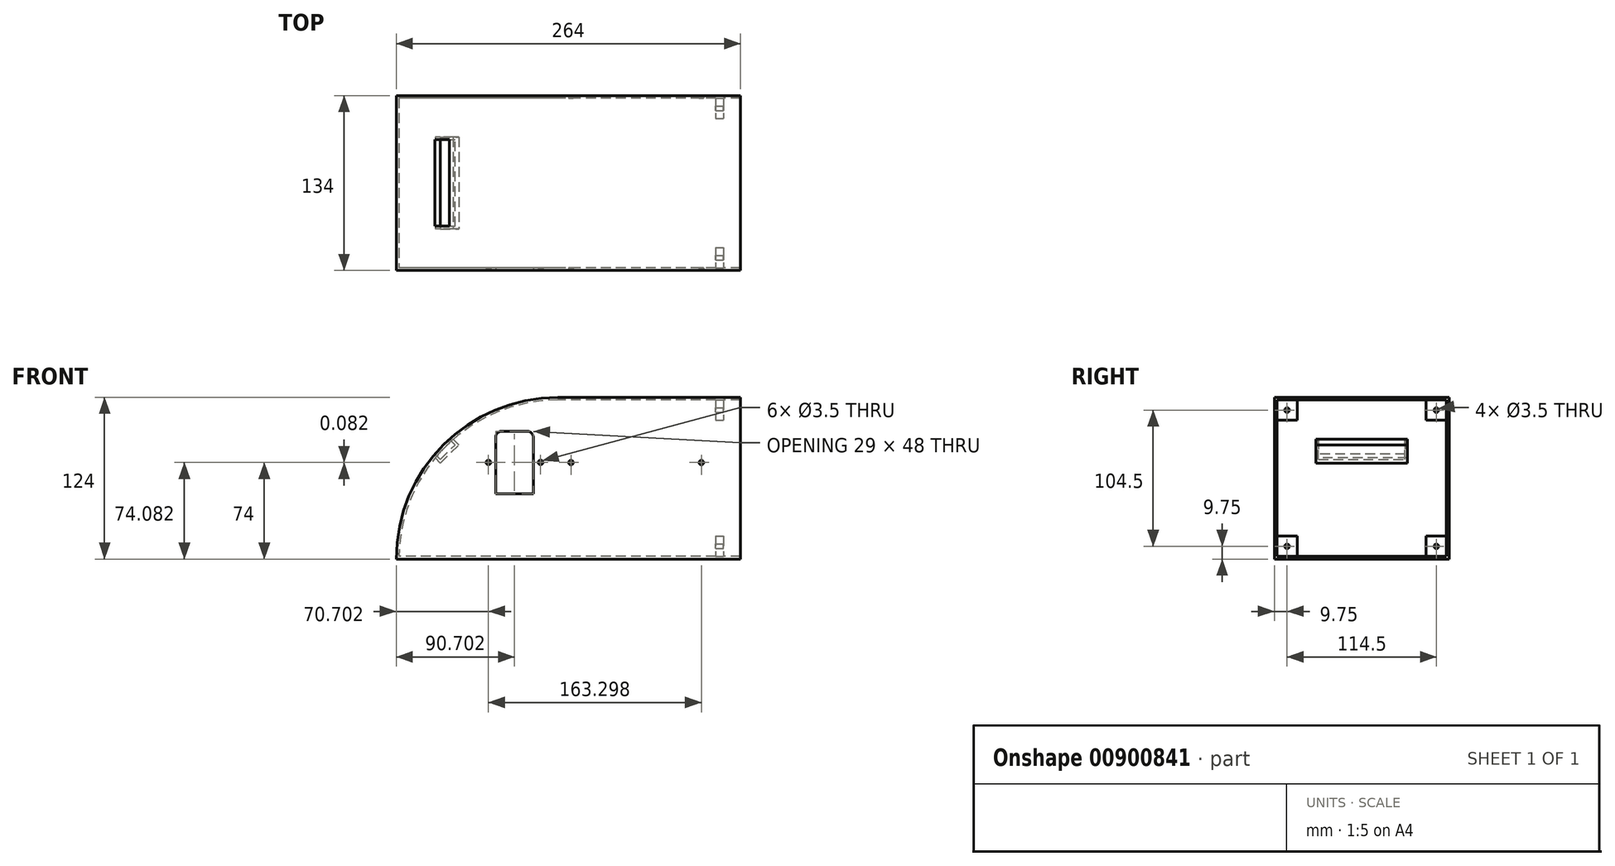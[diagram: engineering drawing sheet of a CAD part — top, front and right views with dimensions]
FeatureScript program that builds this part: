
annotation { "Feature Type Name" : "Feature", "Feature Type Description" : "" }
export const myFeature = defineFeature(function(context is Context, id is Id, definition is map)
    precondition{}
    {
        {
            var Q0;
            Q0=qCreatedBy(makeId("Top.planeOp"),FACE);
            var sketch = newSketch(context, id + "F0", { "sketchPlane" : qUnion([Q0])});
            skLineSegment(sketch, "E0.bottom", {"start": v(132, 67) * mm, "end": v(-132, 67) * mm});
            skLineSegment(sketch, "E0.top", {"start": v(132, -67) * mm, "end": v(-132, -67) * mm});
            skLineSegment(sketch, "E0.left", {"start": v(132, 67) * mm, "end": v(132, -67) * mm});
            skLineSegment(sketch, "E0.right", {"start": v(-132, 67) * mm, "end": v(-132, -67) * mm});
            skPoint(sketch, "E0.middle", {"position": v(0, 0) * mm});
            skSolve(sketch);
        }
        {
            var Q0;
            Q0 = qSketchRegion(id + "F0", true);
            extrude(context, id + "F1", {"entities" : qUnion([Q0]), "endBound" : BoundingType.SYMMETRIC, "depth" : 124 * mm, "offsetDistance" : 25 * mm});
        }
        {
            var Q0;
            Q0=makeQuery(id+"F1.opExtrude","SWEPT_FACE",FACE,{"disambiguationData":[OSD([sQuery(id+"F0.wireOp",EDGE,"E0.top")])]});
            var sketch = newSketch(context, id + "F2", { "sketchPlane" : qUnion([Q0])});
            skLineSegment(sketch, "E1.left", {"start": v(132, 62) * mm, "end": v(132, -47.6) * mm});
            skLineSegment(sketch, "E2.top", {"start": v(-132, -62) * mm, "end": v(-8, -62) * mm});
            skLineSegment(sketch, "E2.left", {"start": v(-132, 62) * mm, "end": v(-132, -62) * mm});
            skArc(sketch, "E3", {"start": v(-8, 62) * mm, "mid": v(-95.68, 25.68) * mm, "end": v(-132, -62) * mm});
            skLineSegment(sketch, "E4", {"start": v(-8, 62) * mm, "end": v(-132, 62) * mm});
            skSolve(sketch);
        }
        {
            var Q0;
            Q0=makeQuery(id+"F2.imprint","IMPRINT",FACE,{"disambiguationData":[TD([[makeQuery(id+"F2.imprint","IMPRINT",EDGE,{"derivedFrom":sQuery(id+"F2.wireOp",EDGE,"E2.left")}),1.0]])]});
            extrude(context, id + "F3", {"entities" : qUnion([Q0]), "operationType" : NewBodyOperationType.REMOVE, "oppositeDirection" : true, "depth" : 150 * mm, "offsetDistance" : 25 * mm});
        }
        {
            var Q0;
            Q0=makeQuery(id+"F1.opExtrude","SWEPT_FACE",FACE,{"disambiguationData":[OSD([sQuery(id+"F0.wireOp",EDGE,"E0.top")])]});
            var sketch = newSketch(context, id + "F4", { "sketchPlane" : qUnion([Q0])});
            skLineSegment(sketch, "E5", {"start": v(-8, 62) * mm, "end": v(-132, -62) * mm, "construction": true});
            skLineSegment(sketch, "E6", {"start": v(-70, 0) * mm, "end": v(-110.64, 40.64) * mm, "construction": true});
            skLineSegment(sketch, "E7", {"start": v(-89.5, 31.02) * mm, "end": v(-81.08, 22.6) * mm});
            skLineSegment(sketch, "E8", {"start": v(-81.08, 22.6) * mm, "end": v(-95.15, 8.53) * mm});
            skLineSegment(sketch, "E9", {"start": v(-95.15, 8.53) * mm, "end": v(-103.57, 16.95) * mm});
            skLineSegment(sketch, "E10", {"start": v(-89.5, 31.02) * mm, "end": v(-103.57, 16.95) * mm, "construction": true});
            skLineSegment(sketch, "E11", {"start": v(-85.29, 26.81) * mm, "end": v(-99.36, 12.74) * mm, "construction": true});
            skLineSegment(sketch, "E12", {"start": v(-96.57, 12.78) * mm, "end": v(-85.32, 24.02) * mm});
            skLineSegment(sketch, "E13", {"start": v(-85.32, 24.02) * mm, "end": v(-90.9, 29.6) * mm});
            skLineSegment(sketch, "E14", {"start": v(-96.57, 12.78) * mm, "end": v(-102.15, 18.36) * mm});
            skLineSegment(sketch, "E15", {"start": v(-102.15, 18.36) * mm, "end": v(-103.57, 16.95) * mm});
            skLineSegment(sketch, "E16", {"start": v(-89.5, 31.02) * mm, "end": v(-90.9, 29.6) * mm});
            skSolve(sketch);
        }
        {
            var Q0;
            Q0 = qSketchRegion(id + "F4", true);
            extrude(context, id + "F5", {"entities" : qUnion([Q0]), "operationType" : NewBodyOperationType.ADD, "oppositeDirection" : true, "depth" : 100.2 * mm, "offsetDistance" : 25 * mm, "hasSecondDirection" : true, "secondDirectionOppositeDirection" : true, "secondDirectionDepth" : 33.8 * mm});
        }
        {
            var Q0;
            Q0=makeQuery(id+"F4.imprint","IMPRINT",FACE,{"disambiguationData":[TD([[makeQuery(id+"F4.imprint","IMPRINT",EDGE,{"derivedFrom":sQuery(id+"F4.wireOp",EDGE,"E7")}),1.0]])]});
            var sketch = newSketch(context, id + "F6", { "sketchPlane" : qUnion([Q0])});
            skLineSegment(sketch, "E17", {"start": v(-8, 62) * mm, "end": v(-132, -62) * mm, "construction": true});
            skLineSegment(sketch, "E18", {"start": v(-70, 0) * mm, "end": v(-110.64, 40.64) * mm, "construction": true});
            skLineSegment(sketch, "E19", {"start": v(-98.1, 14.32) * mm, "end": v(-86.86, 25.56) * mm});
            skLineSegment(sketch, "E20", {"start": v(-86.86, 25.56) * mm, "end": v(-93.94, 32.63) * mm});
            skLineSegment(sketch, "E21", {"start": v(-98.1, 14.32) * mm, "end": v(-105.18, 21.39) * mm});
            skLineSegment(sketch, "E22", {"start": v(-93.94, 32.63) * mm, "end": v(-105.18, 21.39) * mm});
            skSolve(sketch);
        }
        {
            var Q0;
            Q0 = qSketchRegion(id + "F6", true);
            extrude(context, id + "F7", {"entities" : qUnion([Q0]), "operationType" : NewBodyOperationType.REMOVE, "oppositeDirection" : true, "depth" : 100.2 * mm, "offsetDistance" : 25 * mm, "hasSecondDirection" : true, "secondDirectionOppositeDirection" : true, "secondDirectionDepth" : 33.8 * mm});
        }
        {
            var Q0;
            Q0=makeQuery(id+"F1.opExtrude","SWEPT_FACE",FACE,{"disambiguationData":[OSD([sQuery(id+"F0.wireOp",EDGE,"E0.left")])]});
            shell(context, id + "F8", {"entities" : qUnion([Q0]), "thickness" : 2 * mm});
        }
        {
            var Q0;
            Q0=makeQuery(id+"F4.imprint","IMPRINT",FACE,{"disambiguationData":[TD([[makeQuery(id+"F4.imprint","IMPRINT",EDGE,{"derivedFrom":sQuery(id+"F4.wireOp",EDGE,"E7")}),1.0]])]});
            var sketch = newSketch(context, id + "F9", { "sketchPlane" : qUnion([Q0])});
            skCircle(sketch, "E23", {"center": v(102, 12) * mm, "radius": 1.75 * mm});
            skCircle(sketch, "E24", {"center": v(2, 12) * mm, "radius": 1.75 * mm});
            skLineSegment(sketch, "E25", {"start": v(2, 12) * mm, "end": v(102, 12) * mm, "construction": true});
            skSolve(sketch);
        }
        {
            var Q0;
            Q0 = qSketchRegion(id + "F9", true);
            extrude(context, id + "F10", {"entities" : qUnion([Q0]), "operationType" : NewBodyOperationType.REMOVE, "endBound" : BoundingType.THROUGH_ALL, "oppositeDirection" : true, "depth" : 25 * mm, "offsetDistance" : 25 * mm});
        }
        {
            var Q0;
            Q0=makeQuery(id+"F4.imprint","IMPRINT",FACE,{"disambiguationData":[TD([[makeQuery(id+"F4.imprint","IMPRINT",EDGE,{"derivedFrom":sQuery(id+"F4.wireOp",EDGE,"E7")}),1.0]])]});
            var sketch = newSketch(context, id + "F11", { "sketchPlane" : qUnion([Q0])});
            skLineSegment(sketch, "E26", {"start": v(4.16, 12.08) * mm, "end": v(-72.87, 12.08) * mm, "construction": true});
            skLineSegment(sketch, "E27.bottom", {"start": v(-31.8, 36.08) * mm, "end": v(-50.8, 36.08) * mm});
            skLineSegment(sketch, "E27.top", {"start": v(-26.8, -11.92) * mm, "end": v(-55.8, -11.92) * mm});
            skLineSegment(sketch, "E27.left", {"start": v(-26.8, 31.08) * mm, "end": v(-26.8, -11.92) * mm});
            skLineSegment(sketch, "E27.right", {"start": v(-55.8, 31.08) * mm, "end": v(-55.8, -11.92) * mm});
            skPoint(sketch, "E27.middle", {"position": v(-41.3, 12.08) * mm});
            skPoint(sketch, "E28.visualSharp", {"position": v(-55.8, 36.08) * mm});
            skArc(sketch, "E28.filletArc", {"start": v(-50.8, 36.08) * mm, "mid": v(-54.33, 34.62) * mm, "end": v(-55.8, 31.08) * mm});
            skPoint(sketch, "E29.visualSharp", {"position": v(-26.8, 36.08) * mm});
            skArc(sketch, "E29.filletArc", {"start": v(-26.8, 31.08) * mm, "mid": v(-28.26, 34.62) * mm, "end": v(-31.8, 36.08) * mm});
            skCircle(sketch, "E30", {"center": v(-61.3, 12.08) * mm, "radius": 1.75 * mm});
            skCircle(sketch, "E31", {"center": v(-21.3, 12.08) * mm, "radius": 1.75 * mm});
            skSolve(sketch);
        }
        {
            var Q0;
            Q0 = qSketchRegion(id + "F11", true);
            extrude(context, id + "F12", {"entities" : qUnion([Q0]), "operationType" : NewBodyOperationType.REMOVE, "oppositeDirection" : true, "depth" : 25 * mm, "offsetDistance" : 25 * mm});
        }
        {
            var Q0;
            Q0=makeQuery(id+"F1.opExtrude","SWEPT_FACE",FACE,{"disambiguationData":[OSD([sQuery(id+"F0.wireOp",EDGE,"E0.left")])]});
            var sketch = newSketch(context, id + "F13", { "sketchPlane" : qUnion([Q0])});
            skLineSegment(sketch, "E32.bottom", {"start": v(-65, 60) * mm, "end": v(-49.5, 60) * mm});
            skLineSegment(sketch, "E32.top", {"start": v(-65, 44.5) * mm, "end": v(-49.5, 44.5) * mm});
            skLineSegment(sketch, "E32.left", {"start": v(-65, 60) * mm, "end": v(-65, 44.5) * mm});
            skLineSegment(sketch, "E32.right", {"start": v(-49.5, 60) * mm, "end": v(-49.5, 44.5) * mm});
            skLineSegment(sketch, "E33", {"start": v(-65, 60) * mm, "end": v(-49.5, 44.5) * mm, "construction": true});
            skCircle(sketch, "E34", {"center": v(-57.25, 52.25) * mm, "radius": 1.75 * mm});
            skLineSegment(sketch, "E35", {"start": v(0, 71.95) * mm, "end": v(0, -67.4) * mm, "construction": true});
            skPoint(sketch, "E35.endSnap0", {"position": v(0, -62) * mm});
            skLineSegment(sketch, "E36", {"start": v(-82.1, 0) * mm, "end": v(87.37, 0) * mm, "construction": true});
            skLineSegment(sketch, "E37.MirrorCS", {"start": v(82.1, 0) * mm, "end": v(-87.37, 0) * mm, "construction": true});
            skLineSegment(sketch, "E38.MirrorCS", {"start": v(49.5, 60) * mm, "end": v(49.5, 44.5) * mm});
            skLineSegment(sketch, "E39.MirrorCS", {"start": v(65, 44.5) * mm, "end": v(49.5, 44.5) * mm});
            skLineSegment(sketch, "E40.MirrorCS", {"start": v(65, 60) * mm, "end": v(49.5, 60) * mm});
            skLineSegment(sketch, "E41.MirrorCS", {"start": v(65, 60) * mm, "end": v(49.5, 44.5) * mm, "construction": true});
            skCircle(sketch, "E42.MirrorC", {"center": v(57.25, 52.25) * mm, "radius": 1.75 * mm});
            skLineSegment(sketch, "E43.MirrorCS", {"start": v(65, 60) * mm, "end": v(65, 44.5) * mm});
            skLineSegment(sketch, "E44.MirrorCS", {"start": v(65, -60) * mm, "end": v(49.5, -44.5) * mm, "construction": true});
            skLineSegment(sketch, "E45.MirrorCS", {"start": v(65, -60) * mm, "end": v(49.5, -60) * mm});
            skLineSegment(sketch, "E46.MirrorCS", {"start": v(0, -71.95) * mm, "end": v(0, 67.4) * mm, "construction": true});
            skLineSegment(sketch, "E47.MirrorCS", {"start": v(65, -44.5) * mm, "end": v(49.5, -44.5) * mm});
            skLineSegment(sketch, "E48.MirrorCS", {"start": v(65, -60) * mm, "end": v(65, -44.5) * mm});
            skLineSegment(sketch, "E49.MirrorCS", {"start": v(-65, -60) * mm, "end": v(-49.5, -44.5) * mm, "construction": true});
            skLineSegment(sketch, "E50.MirrorCS", {"start": v(-65, -60) * mm, "end": v(-49.5, -60) * mm});
            skCircle(sketch, "E51.MirrorC", {"center": v(-57.25, -52.25) * mm, "radius": 1.75 * mm});
            skCircle(sketch, "E52.MirrorC", {"center": v(57.25, -52.25) * mm, "radius": 1.75 * mm});
            skLineSegment(sketch, "E53.MirrorCS", {"start": v(-65, -44.5) * mm, "end": v(-49.5, -44.5) * mm});
            skLineSegment(sketch, "E54.MirrorCS", {"start": v(49.5, -60) * mm, "end": v(49.5, -44.5) * mm});
            skLineSegment(sketch, "E55.MirrorCS", {"start": v(-65, -60) * mm, "end": v(-65, -44.5) * mm});
            skLineSegment(sketch, "E56.MirrorCS", {"start": v(-49.5, -60) * mm, "end": v(-49.5, -44.5) * mm});
            skSolve(sketch);
        }
        {
            var Q0;
            Q0 = qSketchRegion(id + "F13", true);
            extrude(context, id + "F14", {"entities" : qUnion([Q0]), "operationType" : NewBodyOperationType.ADD, "oppositeDirection" : true, "depth" : 19 * mm, "offsetDistance" : 25 * mm, "hasSecondDirection" : true, "secondDirectionOppositeDirection" : true, "secondDirectionDepth" : 13 * mm});
        }
    });
